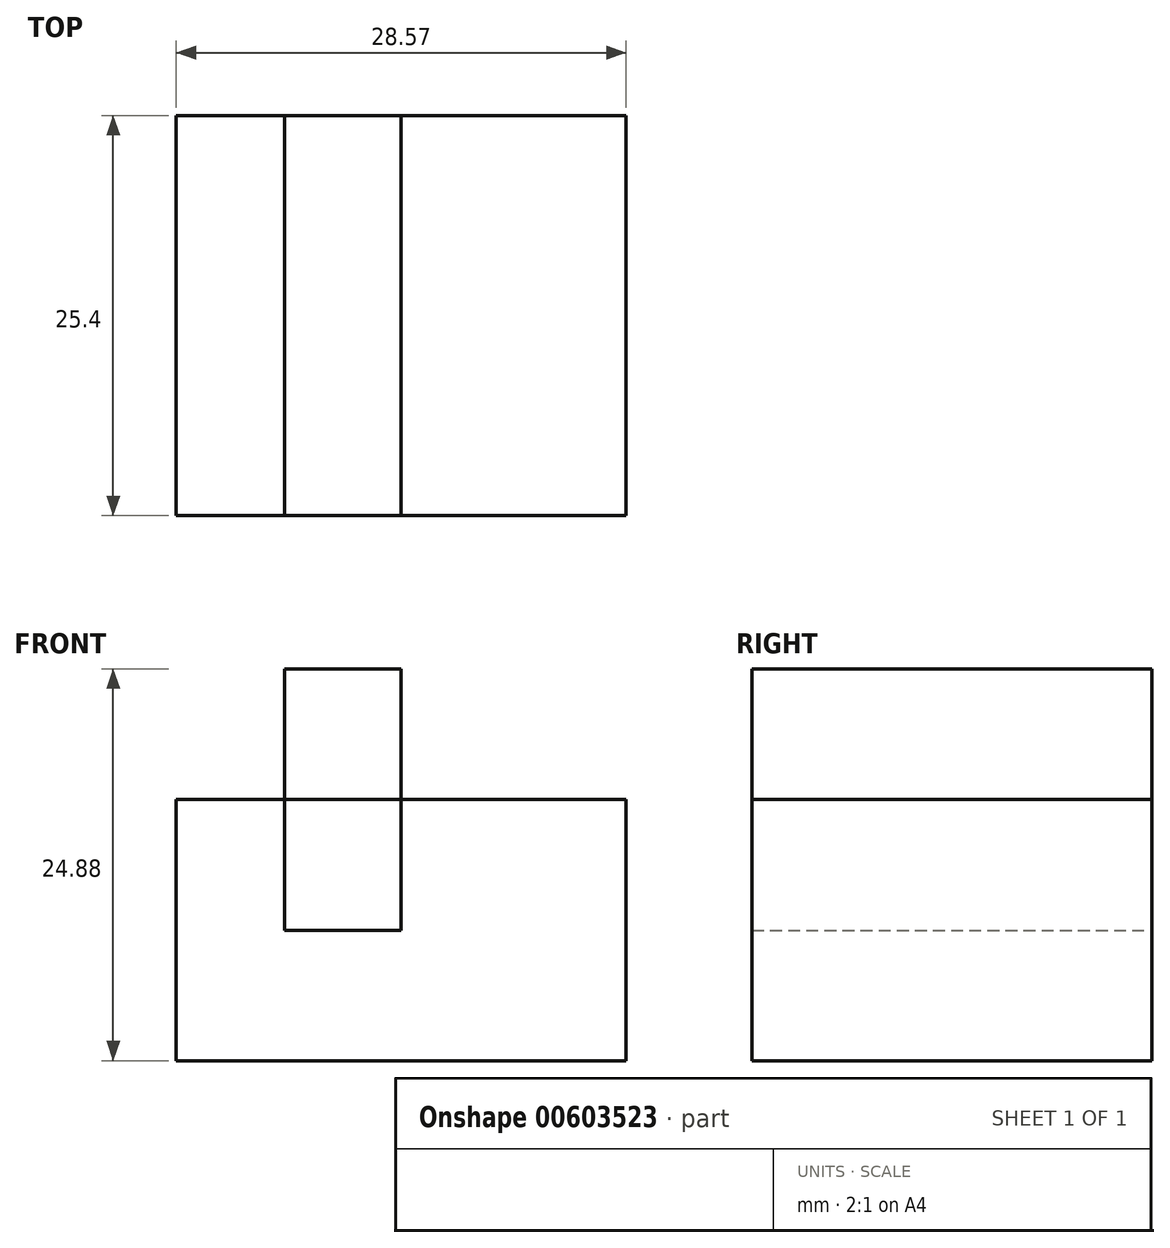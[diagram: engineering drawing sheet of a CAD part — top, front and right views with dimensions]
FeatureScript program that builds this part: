
annotation { "Feature Type Name" : "Feature", "Feature Type Description" : "" }
export const myFeature = defineFeature(function(context is Context, id is Id, definition is map)
    precondition{}
    {
        {
            var Q0;
            Q0=qCreatedBy(makeId("Front.planeOp"),FACE);
            var sketch = newSketch(context, id + "F0", { "sketchPlane" : qUnion([Q0])});
            skLineSegment(sketch, "E0.bottom", {"start": v(44.7, -34.74) * mm, "end": v(-44.7, -34.74) * mm});
            skLineSegment(sketch, "E0.top", {"start": v(44.7, 34.74) * mm, "end": v(-44.7, 34.74) * mm});
            skLineSegment(sketch, "E0.left", {"start": v(44.7, -34.74) * mm, "end": v(44.7, 34.74) * mm});
            skLineSegment(sketch, "E0.right", {"start": v(-44.7, -34.74) * mm, "end": v(-44.7, 34.74) * mm});
            skPoint(sketch, "E0.middle", {"position": v(0, 0) * mm});
            skLineSegment(sketch, "E1.bottom", {"start": v(89.84, 67.34) * mm, "end": v(61.27, 67.34) * mm});
            skLineSegment(sketch, "E1.top", {"start": v(89.84, 50.76) * mm, "end": v(61.27, 50.76) * mm});
            skLineSegment(sketch, "E1.left", {"start": v(89.84, 67.34) * mm, "end": v(89.84, 50.76) * mm});
            skLineSegment(sketch, "E1.right", {"start": v(61.27, 67.34) * mm, "end": v(61.27, 50.76) * mm});
            skPoint(sketch, "E1.middle", {"position": v(75.56, 59.05) * mm});
            skLineSegment(sketch, "E2.bottom", {"start": v(86.7, 67.34) * mm, "end": v(71.85, 67.34) * mm});
            skLineSegment(sketch, "E2.top", {"start": v(86.7, 67.34) * mm, "end": v(71.85, 67.34) * mm});
            skLineSegment(sketch, "E2.left", {"start": v(86.7, 67.34) * mm, "end": v(86.7, 67.34) * mm});
            skLineSegment(sketch, "E2.right", {"start": v(71.85, 67.34) * mm, "end": v(71.85, 67.34) * mm});
            skPoint(sketch, "E2.middle", {"position": v(79.27, 67.34) * mm});
            skLineSegment(sketch, "E3.bottom", {"start": v(75.56, 59.05) * mm, "end": v(68.13, 59.05) * mm});
            skLineSegment(sketch, "E3.top", {"start": v(75.56, 75.64) * mm, "end": v(68.13, 75.64) * mm});
            skLineSegment(sketch, "E3.left", {"start": v(75.56, 59.05) * mm, "end": v(75.56, 75.64) * mm});
            skLineSegment(sketch, "E3.right", {"start": v(68.13, 59.05) * mm, "end": v(68.13, 75.64) * mm});
            skPoint(sketch, "E3.middle", {"position": v(71.85, 67.34) * mm});
            skLineSegment(sketch, "E4.bottom", {"start": v(-246.6, 56.1) * mm, "end": v(-250.02, 56.1) * mm});
            skLineSegment(sketch, "E4.top", {"start": v(-246.6, 62) * mm, "end": v(-250.02, 62) * mm});
            skLineSegment(sketch, "E4.left", {"start": v(-246.6, 56.1) * mm, "end": v(-246.6, 62) * mm});
            skLineSegment(sketch, "E4.right", {"start": v(-250.02, 56.1) * mm, "end": v(-250.02, 62) * mm});
            skPoint(sketch, "E4.middle", {"position": v(-248.3, 59.05) * mm});
            skPoint(sketch, "E4.middle.positionSnap0", {"position": v(71.85, 59.05) * mm});
            skPoint(sketch, "E4.centerSnap0", {"position": v(71.85, 59.05) * mm});
            skLineSegment(sketch, "E5.bottom", {"start": v(-246.6, 56.1) * mm, "end": v(-246.6, 56.1) * mm});
            skLineSegment(sketch, "E5.top", {"start": v(-246.6, 62) * mm, "end": v(-246.6, 62) * mm});
            skPoint(sketch, "E5.middle", {"position": v(-246.6, 59.05) * mm});
            skSolve(sketch);
        }
        {
            var Q0;
            Q0=makeQuery(id+"F0.imprint","IMPRINT",FACE,{"disambiguationData":[TD([[makeQuery(id+"F0.imprint","IMPRINT",EDGE,{"derivedFrom":sQuery(id+"F0.wireOp",EDGE,"E1.top")}),-1.0]])]});
            var Q1;
            {var subQ0=sQuery(id+"F0.wireOp",EDGE,"E3.top");Q1=makeQuery(id+"F0.imprint","IMPRINT",FACE,{"disambiguationData":[TD([[makeQuery(id+"F0.imprint","IMPRINT",EDGE,{"derivedFrom":subQ0}),1.0]])]});}
            extrude(context, id + "F1", {"entities" : qUnion([Q0, Q1]), "depth" : 25.4 * mm, "offsetDistance" : 25.4 * mm});
        }
    });
